# Revit family: surface no interlocked sockets 380_415V
name_source: partatom
category: Installations électriques
revit_build: Autodesk Revit 2018 (Build: 20170223_1515(x64)
units: mm (PartAtom-declared; Revit-internal decimal feet)

## family parameters
Conserver l'orientation des annotations = Non
Cote de connecteur circulaire = Utiliser le diamètre
Couper avec des vides une fois chargée = Non
Hôte = Face
Partagée = Non
Point de calcul de pièce = Non
Type d'élément = Normal

## types (18) — shared parameters
Elévation par défaut = 1000 mm  [stored 3.28084 ft]
Fabricant = Legrand
International standard socket for flush mounting or surface mounting with accessory allows the connection of power devices = International standard socket for flush mounting or surface mounting with accessory allows the connection of power devices
Maximum use temperature = 40
Minimum installation temperature = -5
Minimum use temperature = -25
Product family = 0854-P17 TEMPRA PRO
Standard IEC or NFC = IEC
Tension V = 400 V  50/60 Hz red
characteristic color = red
connecting type = screw terminals
interlocking type = x
material of box = plastic
resistance to chocks IK = 9

## per-type parameters (varying)
| type | Description | Diameter cable entry | Modèle | Number of poles | Position of earth h | depth mm | halogen free | height mm | horizontal fixing distance mm | intensity A | protection class IP | vertical fixing distance mm | width mm |
| IDS_LG_090159 | IDS_DESCRIPTION_LG_090159 | M20/M25 | LG-090159 | 4 | 6 | 147 mm | Oui | 147 mm | 70 mm | 16 A | IP44 | 0 mm  [stored 0 ft] | 93 mm  [stored 0.305118 ft] |
| IDS_LG_090160 | IDS_DESCRIPTION_LG_090160 | M20/M25 | LG-090160 | 5 | 6 | 153 mm  [stored 0.501969 ft] | Oui | 147 mm | 70 mm | 16 A | IP44 | 0 mm  [stored 0 ft] | 93 mm  [stored 0.305118 ft] |
| IDS_LG_090161 | IDS_DESCRIPTION_LG_090161 | M25/M32 | LG-090161 | 4 | 6 | 172 mm | Oui | 174 mm  [stored 0.570866 ft] | 90 mm | 32 A | IP44 | 0 mm  [stored 0 ft] | 113 mm  [stored 0.370735 ft] |
| IDS_LG_090162 | IDS_DESCRIPTION_LG_090162 | M25/M32 | LG-090162 | 5 | 6 | 177 mm | Oui | 174 mm  [stored 0.570866 ft] | 90 mm | 32 A | IP44 | 0 mm  [stored 0 ft] | 113 mm  [stored 0.370735 ft] |
| IDS_LG_555157 | IDS_DESCRIPTION_LG_555157 | M20/M25 | LG-555157 | 3 | 9 | 125 mm  [stored 0.410105 ft] | Oui | 131 mm  [stored 0.42979 ft] | 70 mm | 16 A | IP44 | 0 mm  [stored 0 ft] | 93 mm  [stored 0.305118 ft] |
| IDS_LG_555158 | IDS_DESCRIPTION_LG_555158 | M20/M25 | LG-555158 | 4 | 6 | 133 mm  [stored 0.436352 ft] | Oui | 131 mm  [stored 0.42979 ft] | 70 mm | 16 A | IP44 | 0 mm  [stored 0 ft] | 93 mm  [stored 0.305118 ft] |
| IDS_LG_555159 | IDS_DESCRIPTION_LG_555159 | M20/M25 | LG-555159 | 5 | 6 | 139 mm | Oui | 131 mm  [stored 0.42979 ft] | 70 mm | 16 A | IP44 | 0 mm  [stored 0 ft] | 93 mm  [stored 0.305118 ft] |
| IDS_LG_555257 | IDS_DESCRIPTION_LG_555257 | M25/M32 | LG-555257 | 3 | 9 | 155 mm | Oui | 156 mm  [stored 0.511811 ft] | 90 mm | 32 A | IP44 | 0 mm  [stored 0 ft] | 113 mm  [stored 0.370735 ft] |
| IDS_LG_555258 | IDS_DESCRIPTION_LG_555258 | M25/M32 | LG-555258 | 4 | 6 | 155 mm | Oui | 156 mm  [stored 0.511811 ft] | 90 mm | 32 A | IP44 | 0 mm  [stored 0 ft] | 113 mm  [stored 0.370735 ft] |
| IDS_LG_555259 | IDS_DESCRIPTION_LG_555259 | M25/M32 | LG-555259 | 5 | 6 | 161 mm | Oui | 156 mm  [stored 0.511811 ft] | 90 mm | 32 A | IP44 | 0 mm  [stored 0 ft] | 113 mm  [stored 0.370735 ft] |
| IDS_LG_555358 | IDS_DESCRIPTION_LG_555358 | M20/M25 | LG-555358 | 4 | 6 | 134 mm  [stored 0.439633 ft] | Non | 138 mm | 70 mm | 16 A |  | 0 mm  [stored 0 ft] | 93 mm  [stored 0.305118 ft] |
| IDS_LG_555359 | IDS_DESCRIPTION_LG_555359 | M20/M25 | LG-555359 | 5 | 6 | 140 mm | Non | 138 mm | 70 mm | 16 A |  | 0 mm  [stored 0 ft] | 93 mm  [stored 0.305118 ft] |
| IDS_LG_555458 | IDS_DESCRIPTION_LG_555458 | M25/M32 | LG-555458 | 4 | 6 | 156 mm  [stored 0.511811 ft] | Non | 163 mm  [stored 0.534777 ft] | 90 mm | 32 A |  | 0 mm  [stored 0 ft] | 113 mm  [stored 0.370735 ft] |
| IDS_LG_555459 | IDS_DESCRIPTION_LG_555459 | M25/M32 | LG-555459 | 5 | 6 | 162 mm | Non | 163 mm  [stored 0.534777 ft] | 90 mm | 32 A |  | 0 mm  [stored 0 ft] | 113 mm  [stored 0.370735 ft] |
| IDS_LG_555658 | IDS_DESCRIPTION_LG_555658 | M20/M40/M50 | LG-555658 | 4 | 6 | 268 mm | Non | 326 mm  [stored 1.06955 ft] | 152 mm | 125 A |  | 260 mm | 170 mm  [stored 0.557743 ft] |
| IDS_LG_555659 | IDS_DESCRIPTION_LG_555659 | M20/M40/M50 | LG-555659 | 5 | 6 | 268 mm | Non | 326 mm  [stored 1.06955 ft] | 152 mm | 125 A |  | 260 mm | 170 mm  [stored 0.557743 ft] |
| IDS_LG_555558 | IDS_DESCRIPTION_LG_555558 | M32 | LG-555558 | 4 | 6 | 190 mm | Non | 270 mm | 119 mm | 63 A |  | 156 mm  [stored 0.511811 ft] | 130 mm |
| IDS_LG_555559 | IDS_DESCRIPTION_LG_555559 | M32 | LG-555559 | 5 | 6 | 190 mm | Non | 270 mm | 119 mm | 63 A |  | 156 mm  [stored 0.511811 ft] | 130 mm |

note: [stored X ft] marks values corroborated as IEEE doubles in the binary element streams (Revit-internal decimal feet)
